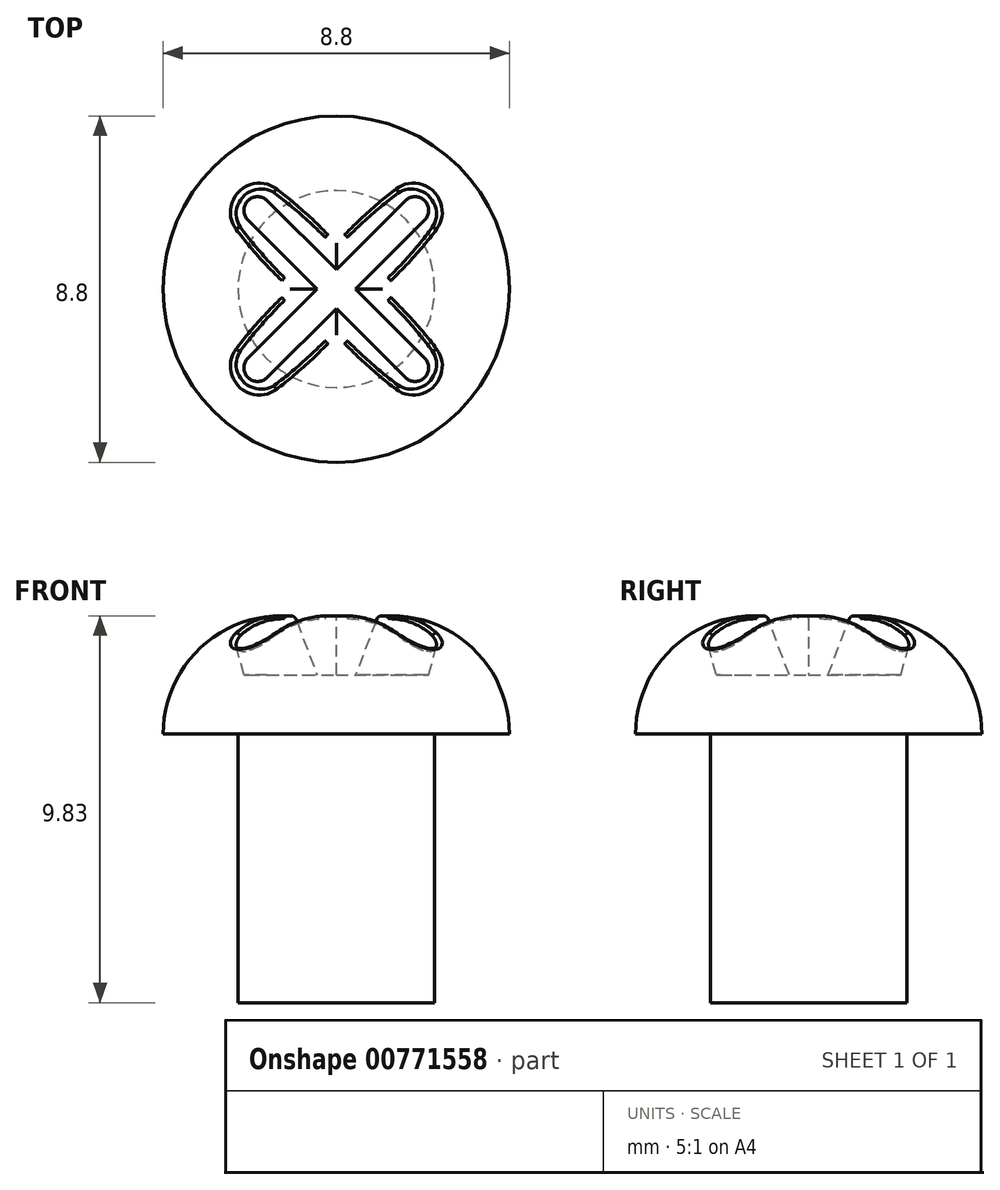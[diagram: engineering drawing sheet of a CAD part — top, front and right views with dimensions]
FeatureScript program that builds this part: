
annotation { "Feature Type Name" : "Feature", "Feature Type Description" : "" }
export const myFeature = defineFeature(function(context is Context, id is Id, definition is map)
    precondition{}
    {
        {
            var Q0;
            Q0=qCreatedBy(makeId("Top.planeOp"),FACE);
            var sketch = newSketch(context, id + "F0", { "sketchPlane" : qUnion([Q0])});
            skCircle(sketch, "E0", {"center": v(0, 0) * mm, "radius": 2.5 * mm});
            skSolve(sketch);
        }
        {
            var Q0;
            Q0 = qSketchRegion(id + "F0", true);
            extrude(context, id + "F1", {"entities" : qUnion([Q0]), "depth" : 6.83 * mm, "offsetDistance" : 25 * mm});
        }
        {
            var Q0;
            Q0=makeQuery(id+"F1.opExtrude","CAP_FACE",FACE,{"disambiguationData":[OSD([sQuery(id+"F0.wireOp",EDGE,"E0")])],"isStart":false});
            var sketch = newSketch(context, id + "F2", { "sketchPlane" : qUnion([Q0])});
            skCircle(sketch, "E1", {"center": v(0, 0) * mm, "radius": 4.4 * mm});
            skSolve(sketch);
        }
        {
            var Q0;
            Q0=makeQuery(id+"F2.imprint","IMPRINT",FACE,{"disambiguationData":[TD([[makeQuery(id+"F2.imprint","IMPRINT",EDGE,{"derivedFrom":sQuery(id+"F2.wireOp",EDGE,"E1")}),1.0]])]});
            var Q1;
            Q1=makeQuery(id+"F2.imprint","IMPRINT",FACE,{"disambiguationData":[TD([[makeQuery(id+"F2.imprint","IMPRINT",EDGE,{"derivedFrom":makeQuery(id+"F1.opExtrude","CAP_EDGE",EDGE,{"disambiguationData":[OSD([sQuery(id+"F0.wireOp",EDGE,"E0")])],"isStart":false})}),1.0]])]});
            extrude(context, id + "F3", {"entities" : qUnion([Q0, Q1]), "operationType" : NewBodyOperationType.ADD, "depth" : 3 * mm, "offsetDistance" : 25 * mm});
        }
        {
            var Q0;
            Q0=makeQuery(id+"F3.opExtrude","CAP_EDGE",EDGE,{"disambiguationData":[OSD([sQuery(id+"F2.wireOp",EDGE,"E1")])],"isStart":false});
            fillet(context, id + "F4", {"entities" : qUnion([Q0]), "radius" : 3 * mm, "tangentPropagation" : true, "allowEdgeOverflow" : false});
        }
        {
            var Q0;
            Q0=makeQuery(id+"F3.opExtrude","CAP_FACE",FACE,{"disambiguationData":[OSD([sQuery(id+"F2.wireOp",EDGE,"E1")])],"isStart":false});
            var sketch = newSketch(context, id + "F5", { "sketchPlane" : qUnion([Q0])});
            skLineSegment(sketch, "E2", {"start": v(-2.3, 0) * mm, "end": v(2.4, 0) * mm, "construction": true});
            skLineSegment(sketch, "E3", {"start": v(0, 2.68) * mm, "end": v(0, -2.44) * mm, "construction": true});
            skLineSegment(sketch, "E4.bottom", {"start": v(2, -2) * mm, "end": v(-2, -2) * mm, "construction": true});
            skLineSegment(sketch, "E4.top", {"start": v(2, 2) * mm, "end": v(-2, 2) * mm, "construction": true});
            skLineSegment(sketch, "E4.left", {"start": v(2, -2) * mm, "end": v(2, 2) * mm, "construction": true});
            skLineSegment(sketch, "E4.right", {"start": v(-2, -2) * mm, "end": v(-2, 2) * mm, "construction": true});
            skPoint(sketch, "E4.middle", {"position": v(0, 0) * mm});
            skLineSegment(sketch, "E5", {"start": v(-2, -2) * mm, "end": v(2, 2) * mm});
            skLineSegment(sketch, "E6", {"start": v(-2, 2) * mm, "end": v(2, -2) * mm});
            skArc(sketch, "E7.0.startCap", {"start": v(-2.53, 1.47) * mm, "mid": v(-2.53, 2.53) * mm, "end": v(-1.47, 2.53) * mm});
            skArc(sketch, "E7.0.endCap", {"start": v(2.53, -1.47) * mm, "mid": v(2.53, -2.53) * mm, "end": v(1.47, -2.53) * mm});
            skLineSegment(sketch, "E7.0.left", {"start": v(-1.47, 2.53) * mm, "end": v(2.53, -1.47) * mm});
            skLineSegment(sketch, "E7.0.right", {"start": v(-2.53, 1.47) * mm, "end": v(1.47, -2.53) * mm});
            skArc(sketch, "E7.1.startCap", {"start": v(-1.47, -2.53) * mm, "mid": v(-2.53, -2.53) * mm, "end": v(-2.53, -1.47) * mm});
            skArc(sketch, "E7.1.endCap", {"start": v(1.47, 2.53) * mm, "mid": v(2.53, 2.53) * mm, "end": v(2.53, 1.47) * mm});
            skLineSegment(sketch, "E7.1.left", {"start": v(-2.53, -1.47) * mm, "end": v(1.47, 2.53) * mm});
            skLineSegment(sketch, "E7.1.right", {"start": v(-1.47, -2.53) * mm, "end": v(2.53, 1.47) * mm});
            skSolve(sketch);
        }
        {
            var Q0;
            Q0 = qSketchRegion(id + "F5", true);
            extrude(context, id + "F6", {"entities" : qUnion([Q0]), "operationType" : NewBodyOperationType.REMOVE, "oppositeDirection" : true, "depth" : 1.5 * mm, "offsetDistance" : 25 * mm, "hasDraft" : true, "draftAngle" : 15 * degree, "draftPullDirection" : true});
        }
        {
            var Q0;
            {var subQ0=sQuery(id+"F5.wireOp",EDGE,"E7.0.right");var subQ1=sQuery(id+"F2.wireOp",EDGE,"E1");Q0=makeQuery(id+"F6.boolean.opBoolean","INTERSECT",EDGE,{"derivedFrom":[makeQuery(id+"F4.opFillet","BLEND_FACE",FACE,{"disambiguationData":[OSD([subQ1])]}),makeQuery(id+"F6.opExtrude","SWEPT_FACE",FACE,{"disambiguationData":[OSD([subQ0]),TDD([makeQuery(id+"F5.imprint","IMPRINT",EDGE,{"disambiguationData":[TD([[makeQuery(id+"F5.imprint","INTERSECT",VERTEX,{"derivedFrom":[subQ0,sQuery(id+"F5.wireOp",EDGE,"E7.1.right")]}),-1.0]])],"derivedFrom":subQ0}),makeQuery(id+"F5.imprint","IMPRINT",EDGE,{"disambiguationData":[TD([[makeQuery(id+"F5.imprint","INTERSECT",VERTEX,{"derivedFrom":[sQuery(id+"F5.wireOp",EDGE,"E7.0.endCap"),subQ0]}),1.0]])],"derivedFrom":subQ0})])]})]});}
            var Q1;
            {var subQ0=sQuery(id+"F5.wireOp",EDGE,"E7.1.right");var subQ1=sQuery(id+"F2.wireOp",EDGE,"E1");Q1=makeQuery(id+"F6.boolean.opBoolean","INTERSECT",EDGE,{"derivedFrom":[makeQuery(id+"F4.opFillet","BLEND_FACE",FACE,{"disambiguationData":[OSD([subQ1])]}),makeQuery(id+"F6.opExtrude","SWEPT_FACE",FACE,{"disambiguationData":[OSD([subQ0]),TDD([makeQuery(id+"F5.imprint","IMPRINT",EDGE,{"disambiguationData":[TD([[makeQuery(id+"F5.imprint","INTERSECT",VERTEX,{"derivedFrom":[sQuery(id+"F5.wireOp",EDGE,"E7.0.left"),subQ0]}),-1.0]])],"derivedFrom":subQ0}),makeQuery(id+"F5.imprint","IMPRINT",EDGE,{"disambiguationData":[TD([[makeQuery(id+"F5.imprint","INTERSECT",VERTEX,{"derivedFrom":[sQuery(id+"F5.wireOp",EDGE,"E7.1.endCap"),subQ0]}),1.0]])],"derivedFrom":subQ0})])]})]});}
            var Q2;
            {var subQ0=sQuery(id+"F5.wireOp",EDGE,"E7.1.left");var subQ1=sQuery(id+"F2.wireOp",EDGE,"E1");Q2=makeQuery(id+"F6.boolean.opBoolean","INTERSECT",EDGE,{"derivedFrom":[makeQuery(id+"F4.opFillet","BLEND_FACE",FACE,{"disambiguationData":[OSD([subQ1])]}),makeQuery(id+"F6.opExtrude","SWEPT_FACE",FACE,{"disambiguationData":[OSD([subQ0]),TDD([makeQuery(id+"F5.imprint","IMPRINT",EDGE,{"disambiguationData":[TD([[makeQuery(id+"F5.imprint","INTERSECT",VERTEX,{"derivedFrom":[sQuery(id+"F5.wireOp",EDGE,"E7.0.left"),subQ0]}),-1.0]])],"derivedFrom":subQ0}),makeQuery(id+"F5.imprint","IMPRINT",EDGE,{"disambiguationData":[TD([[makeQuery(id+"F5.imprint","INTERSECT",VERTEX,{"derivedFrom":[sQuery(id+"F5.wireOp",EDGE,"E7.1.endCap"),subQ0]}),1.0]])],"derivedFrom":subQ0})])]})]});}
            var Q3;
            {var subQ0=sQuery(id+"F5.wireOp",EDGE,"E7.0.left");var subQ1=sQuery(id+"F2.wireOp",EDGE,"E1");Q3=makeQuery(id+"F6.boolean.opBoolean","INTERSECT",EDGE,{"derivedFrom":[makeQuery(id+"F4.opFillet","BLEND_FACE",FACE,{"disambiguationData":[OSD([subQ1])]}),makeQuery(id+"F6.opExtrude","SWEPT_FACE",FACE,{"disambiguationData":[OSD([subQ0]),TDD([makeQuery(id+"F5.imprint","IMPRINT",EDGE,{"disambiguationData":[TD([[makeQuery(id+"F5.imprint","INTERSECT",VERTEX,{"derivedFrom":[sQuery(id+"F5.wireOp",EDGE,"E7.0.startCap"),subQ0]}),-1.0]])],"derivedFrom":subQ0}),makeQuery(id+"F5.imprint","IMPRINT",EDGE,{"disambiguationData":[TD([[makeQuery(id+"F5.imprint","INTERSECT",VERTEX,{"derivedFrom":[subQ0,sQuery(id+"F5.wireOp",EDGE,"E7.1.left")]}),1.0]])],"derivedFrom":subQ0})])]})]});}
            var Q4;
            {var subQ0=sQuery(id+"F5.wireOp",EDGE,"E7.1.left");var subQ1=sQuery(id+"F2.wireOp",EDGE,"E1");Q4=makeQuery(id+"F6.boolean.opBoolean","INTERSECT",EDGE,{"derivedFrom":[makeQuery(id+"F4.opFillet","BLEND_FACE",FACE,{"disambiguationData":[OSD([subQ1])]}),makeQuery(id+"F6.opExtrude","SWEPT_FACE",FACE,{"disambiguationData":[OSD([subQ0]),TDD([makeQuery(id+"F5.imprint","IMPRINT",EDGE,{"disambiguationData":[TD([[makeQuery(id+"F5.imprint","INTERSECT",VERTEX,{"derivedFrom":[sQuery(id+"F5.wireOp",EDGE,"E7.1.startCap"),subQ0]}),-1.0]])],"derivedFrom":subQ0}),makeQuery(id+"F5.imprint","IMPRINT",EDGE,{"disambiguationData":[TD([[makeQuery(id+"F5.imprint","INTERSECT",VERTEX,{"derivedFrom":[sQuery(id+"F5.wireOp",EDGE,"E7.0.right"),subQ0]}),1.0]])],"derivedFrom":subQ0})])]})]});}
            fillet(context, id + "F7", {"entities" : qUnion([Q0, Q1, Q2, Q3, Q4]), "radius" : 0.1 * mm, "tangentPropagation" : true, "allowEdgeOverflow" : false});
        }
    });
